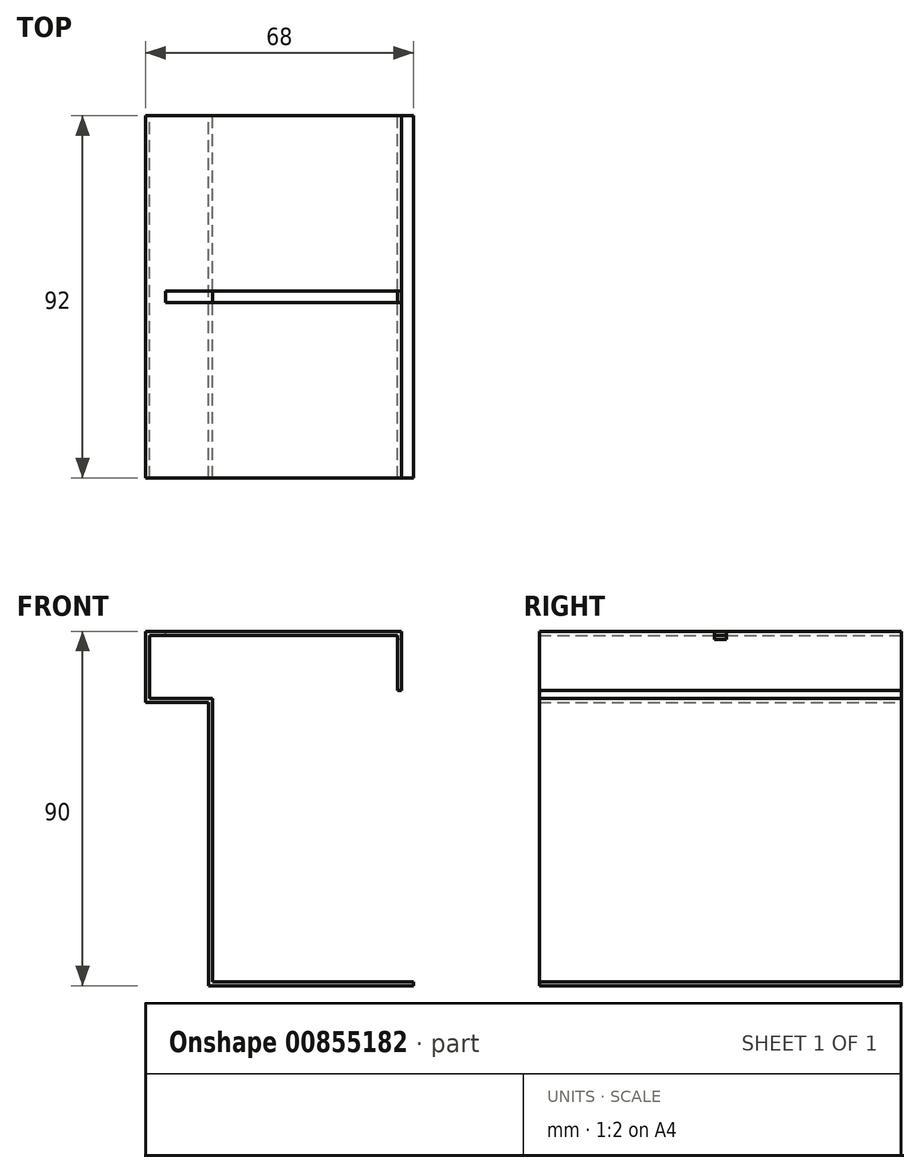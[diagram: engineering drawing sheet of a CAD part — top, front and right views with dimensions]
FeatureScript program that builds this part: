
annotation { "Feature Type Name" : "Feature", "Feature Type Description" : "" }
export const myFeature = defineFeature(function(context is Context, id is Id, definition is map)
    precondition{}
    {
        {
            var Q0;
            Q0=qCreatedBy(makeId("Front.planeOp"),FACE);
            var sketch = newSketch(context, id + "F0", { "sketchPlane" : qUnion([Q0])});
            skLineSegment(sketch, "E0", {"start": v(-36.7, 37.95) * mm, "end": v(28.3, 37.95) * mm});
            skLineSegment(sketch, "E1", {"start": v(28.3, 37.95) * mm, "end": v(28.3, 22.95) * mm});
            skLineSegment(sketch, "E2", {"start": v(-36.7, 37.95) * mm, "end": v(-36.7, 19.95) * mm});
            skLineSegment(sketch, "E3", {"start": v(-36.7, 19.95) * mm, "end": v(-20.7, 19.95) * mm});
            skLineSegment(sketch, "E4", {"start": v(-20.7, 19.95) * mm, "end": v(-20.7, -52.05) * mm});
            skLineSegment(sketch, "E5", {"start": v(-20.7, -52.05) * mm, "end": v(31.3, -52.05) * mm});
            skLineSegment(sketch, "E6.0", {"start": v(27.3, 36.95) * mm, "end": v(27.3, 22.95) * mm});
            skLineSegment(sketch, "E6.1", {"start": v(-35.7, 36.95) * mm, "end": v(27.3, 36.95) * mm});
            skLineSegment(sketch, "E6.2", {"start": v(-19.7, -51.05) * mm, "end": v(31.3, -51.05) * mm});
            skLineSegment(sketch, "E6.3", {"start": v(-19.7, 20.95) * mm, "end": v(-19.7, -51.05) * mm});
            skLineSegment(sketch, "E6.4", {"start": v(-35.7, 20.95) * mm, "end": v(-19.7, 20.95) * mm});
            skLineSegment(sketch, "E6.5", {"start": v(-35.7, 36.95) * mm, "end": v(-35.7, 20.95) * mm});
            skLineSegment(sketch, "E7", {"start": v(27.3, 22.95) * mm, "end": v(28.3, 22.95) * mm});
            skLineSegment(sketch, "E8", {"start": v(31.3, -52.05) * mm, "end": v(31.3, -51.05) * mm});
            skSolve(sketch);
        }
        {
            var Q0;
            Q0=makeQuery(id+"F0.imprint","IMPRINT",FACE,{"disambiguationData":[TD([[makeQuery(id+"F0.imprint","IMPRINT",EDGE,{"derivedFrom":sQuery(id+"F0.wireOp",EDGE,"E0")}),-1.0]])]});
            extrude(context, id + "F1", {"entities" : qUnion([Q0]), "depth" : 92 * mm, "offsetDistance" : 25 * mm});
        }
        {
            var Q0;
            Q0=makeQuery(id+"F1.opExtrude","SWEPT_FACE",FACE,{"disambiguationData":[OSD([sQuery(id+"F0.wireOp",EDGE,"E0")])]});
            var sketch = newSketch(context, id + "F2", { "sketchPlane" : qUnion([Q0])});
            skLineSegment(sketch, "E9.top", {"start": v(28.3, -47.5) * mm, "end": v(-31.7, -47.5) * mm});
            skLineSegment(sketch, "E9.left", {"start": v(28.3, -46) * mm, "end": v(28.3, -47.5) * mm});
            skLineSegment(sketch, "E9.right", {"start": v(-31.7, -46) * mm, "end": v(-31.7, -47.5) * mm});
            skLineSegment(sketch, "E10.top", {"start": v(28.3, -44.5) * mm, "end": v(-31.7, -44.5) * mm});
            skLineSegment(sketch, "E10.left", {"start": v(28.3, -46) * mm, "end": v(28.3, -44.5) * mm});
            skLineSegment(sketch, "E10.right", {"start": v(-31.7, -46) * mm, "end": v(-31.7, -44.5) * mm});
            skSolve(sketch);
        }
        {
            var Q0;
            Q0 = qSketchRegion(id + "F2", true);
            extrude(context, id + "F3", {"entities" : qUnion([Q0]), "operationType" : NewBodyOperationType.REMOVE, "oppositeDirection" : true, "depth" : 2 * mm, "offsetDistance" : 25 * mm});
        }
    });
